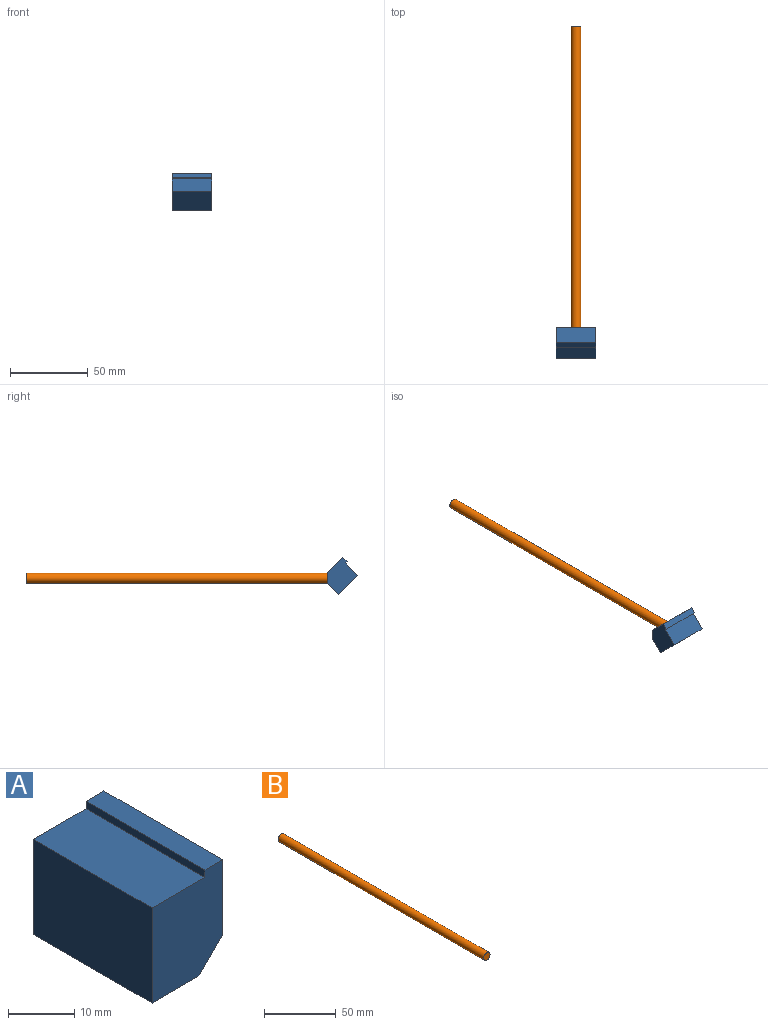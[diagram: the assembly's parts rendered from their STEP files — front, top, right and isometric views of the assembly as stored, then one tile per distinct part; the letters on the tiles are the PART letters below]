
ASSEMBLY  parts=2 mates=1
PART A: 11 faces, bbox 15.1x25.4x19 mm
  f0: plane 25.4x11.3mm, normal (0,0,1), area 287.1mm2, adj f1,f5,f6,f7
  f1: plane 25.4x17.59mm, normal (-1,0,0), area 446.8mm2, adj f0,f2,f6,f7
  f2: plane 25.4x10.02mm, normal (0,0,-1), area 254.5mm2, adj f1,f6,f7,f8
  f3: plane 25.4x13.91mm, normal (1,0,0), area 353.2mm2, adj f4,f6,f7,f8
  f4: plane 25.4x3.8mm, normal (0,0,1), area 96.5mm2, adj f3,f5,f6,f7
  f5: plane 25.4x1.4mm, normal (-1,0,0), area 35.5mm2, adj f0,f4,f6,f7
  f6: plane 18.99x15.1mm, normal (0,-1,0), area 258mm2, adj f0,f1,f2,f3,f4,f5,f8
  f7: plane 18.99x15.1mm, normal (0,1,0), area 258mm2, adj f0,f1,f2,f3,f4,f5,f8
  f8: plane 25.4x5.08mm, normal (0.71,0,-0.71), area 150.8mm2, adj f2,f3,f6,f7,f10
  f9: cone r=0mm half-angle=59deg, axis (0.71,0,-0.71), area 36.9mm2, adj f10
  f10: cylinder r=3.17mm len=11.23mm, axis (0.71,0,-0.71), area 190mm2, adj f8,f9
PART B: 3 faces, bbox 6.4x203.2x6.4 mm
  f0: plane 6.35x6.35mm, normal (0,-1,0), area 31.7mm2, adj f2
  f1: plane 6.35x6.35mm, normal (0,1,0), area 31.7mm2, adj f2
  f2: cylinder r=3.17mm len=203.2mm, axis (0,1,0), area 4053.7mm2, adj f0,f1
PLACE A rot(axis=(0.36,-0.36,0.86),98.4deg) t=(3.18,3.36,-11.67)mm
PLACE B t=(0,1.91,0)mm
MATE fastened B.f2 <-> A.f10  axis (0,-1,0) through (3.18,1.91,0)mm
